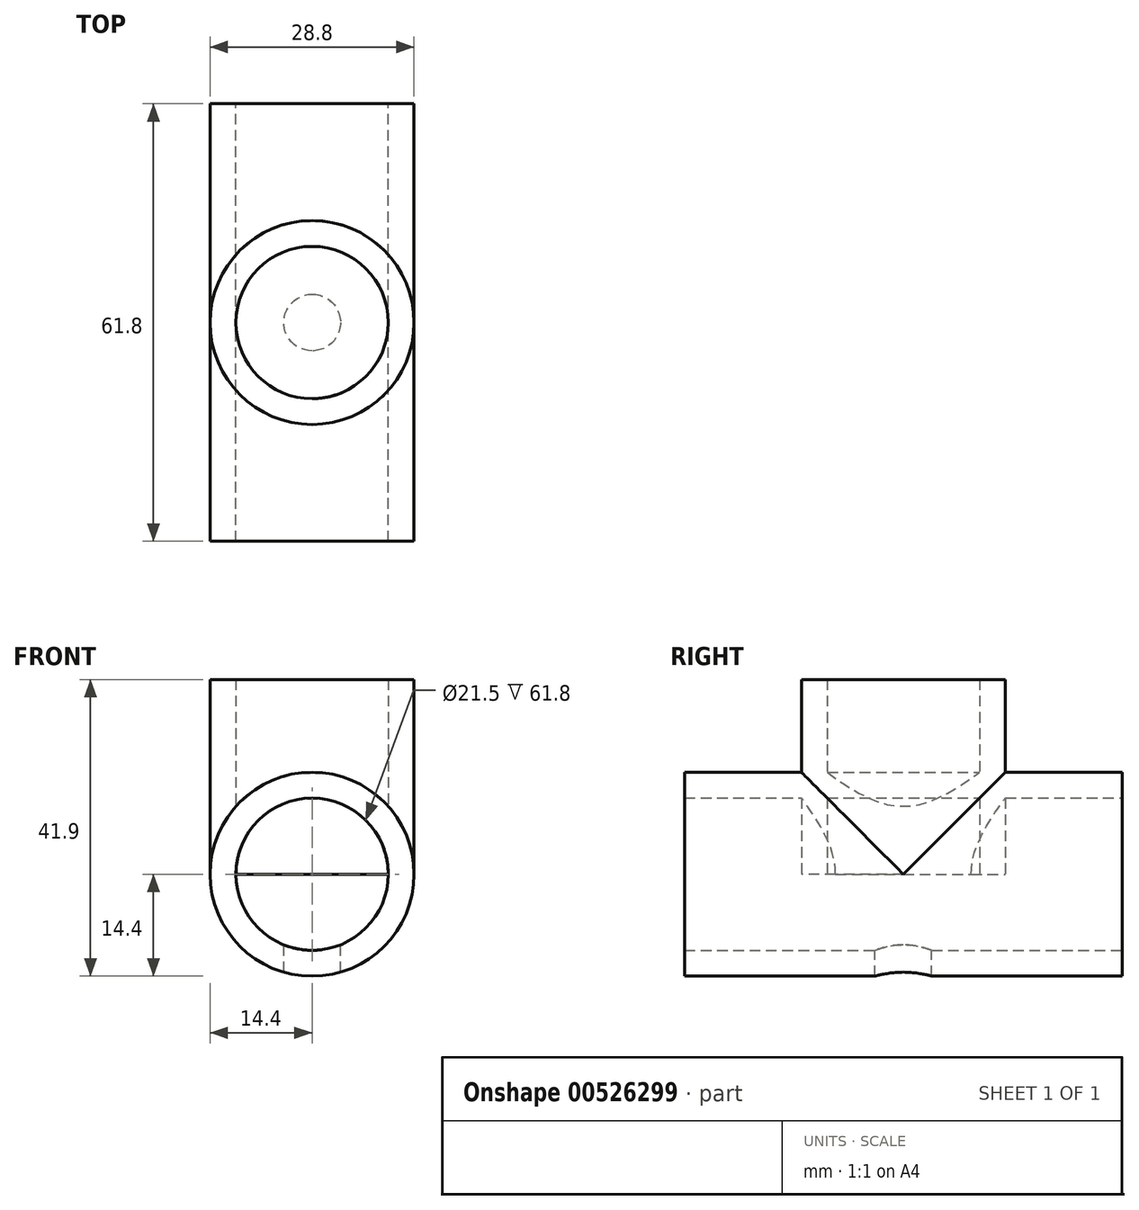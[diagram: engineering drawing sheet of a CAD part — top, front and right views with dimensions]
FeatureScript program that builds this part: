
annotation { "Feature Type Name" : "Feature", "Feature Type Description" : "" }
export const myFeature = defineFeature(function(context is Context, id is Id, definition is map)
    precondition{}
    {
        {
            var Q0;
            Q0=qCreatedBy(makeId("Front.planeOp"),FACE);
            var sketch = newSketch(context, id + "F0", { "sketchPlane" : qUnion([Q0])});
            skCircle(sketch, "E0", {"center": v(0, 0) * mm, "radius": 14.4 * mm});
            skCircle(sketch, "E1", {"center": v(0, 0) * mm, "radius": 10.75 * mm});
            skSolve(sketch);
        }
        {
            var Q0;
            Q0=qSketchRegion(id+"F0",true);
            extrude(context, id + "F1", {"entities" : qUnion([Q0]), "depth" : 61.8 * mm, "offsetDistance" : 25 * mm});
        }
        {
            var Q0;
            Q0=qCreatedBy(makeId("Top.planeOp"),FACE);
            var sketch = newSketch(context, id + "F2", { "sketchPlane" : qUnion([Q0])});
            skLineSegment(sketch, "E2", {"start": v(0, 0) * mm, "end": v(0, -72.1) * mm, "construction": true});
            skPoint(sketch, "E3", {"position": v(0, -30.9) * mm});
            skCircle(sketch, "E4", {"center": v(0, -30.9) * mm, "radius": 10.75 * mm});
            skCircle(sketch, "E5", {"center": v(0, -30.9) * mm, "radius": 14.4 * mm});
            skSolve(sketch);
        }
        {
            var Q0;
            Q0=qSketchRegion(id+"F2",true);
            extrude(context, id + "F3", {"entities" : qUnion([Q0]), "operationType" : NewBodyOperationType.ADD, "depth" : 27.5 * mm, "offsetDistance" : 25 * mm});
        }
        {
            var Q0;
            Q0=qCreatedBy(makeId("Top.planeOp"),FACE);
            var sketch = newSketch(context, id + "F4", { "sketchPlane" : qUnion([Q0])});
            skPoint(sketch, "E6", {"position": v(0, -30.9) * mm});
            skSolve(sketch);
        }
        {
            var Q0;
            Q0=sQuery(id+"F4.wireOp",VERTEX,"E6");
            var Q1;
            Q1=makeQuery(id+"F1.opExtrude","SWEPT_BODY",BODY,{"disambiguationData":[OSD([sQuery(id+"F0.wireOp",EDGE,"E0"),sQuery(id+"F0.wireOp",EDGE,"E1")])]});
            hole(context, id + "F5", {"style" : HoleStyle.SIMPLE, "endStyle" : HoleEndStyle.THROUGH, "holeDiameter" : 8 * mm, "isTappedThrough" : true, "tappedDepth" : 12 * mm, "tapClearance" : 3, "locations" : qUnion([Q0]), "scope" : qUnion([Q1])});
        }
    });
